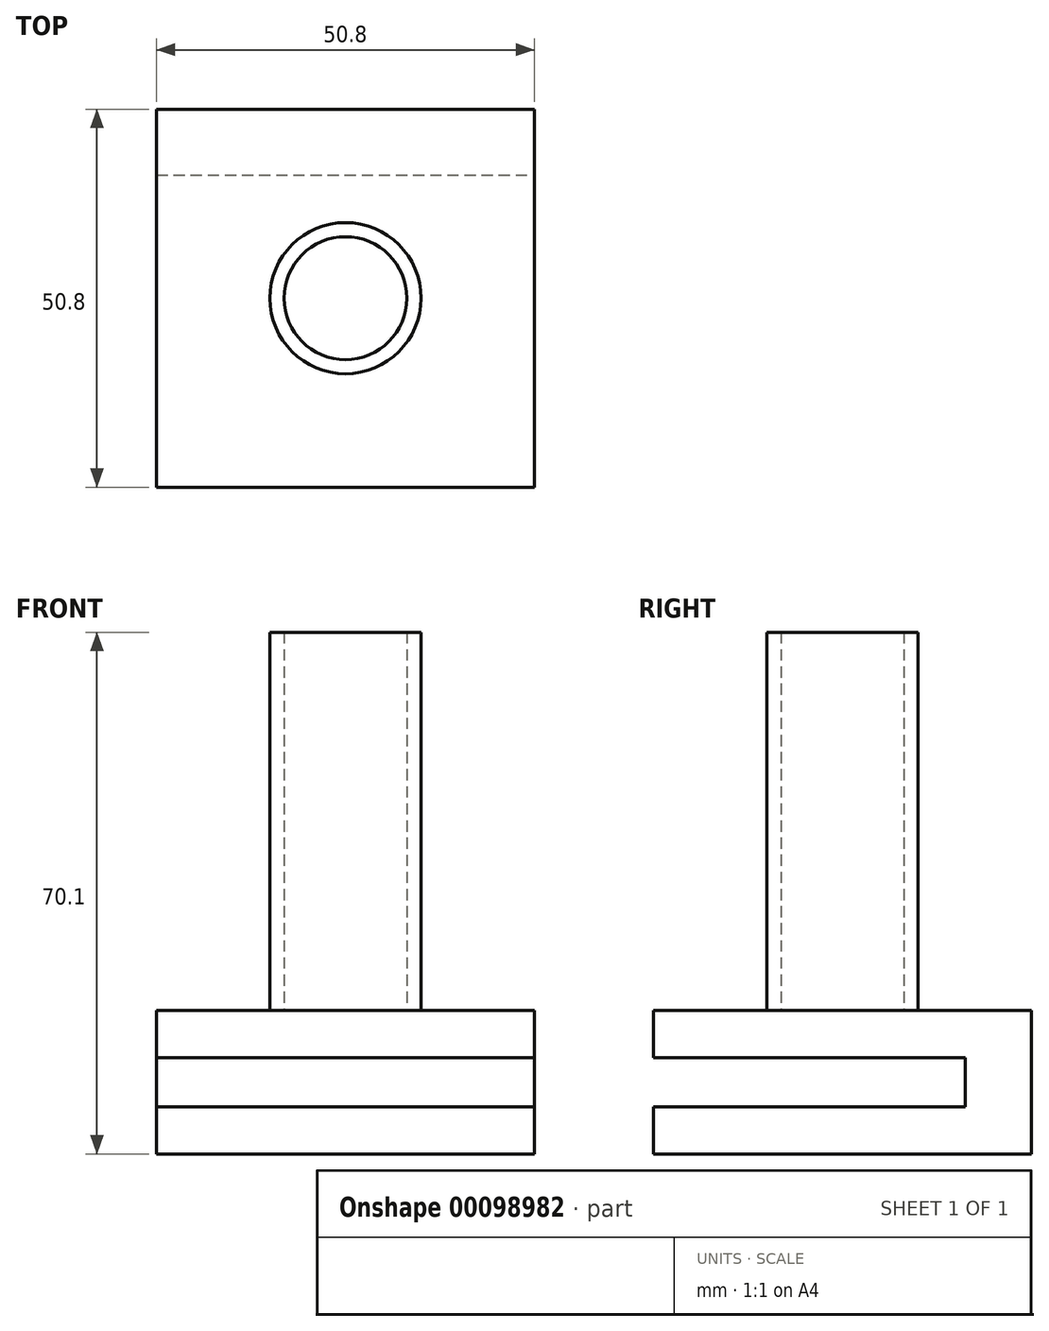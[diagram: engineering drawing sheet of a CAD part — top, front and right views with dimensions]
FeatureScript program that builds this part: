
annotation { "Feature Type Name" : "Feature", "Feature Type Description" : "" }
export const myFeature = defineFeature(function(context is Context, id is Id, definition is map)
    precondition{}
    {
        {
            var Q0;
            Q0=qCreatedBy(makeId("Top.planeOp"),FACE);
            var sketch = newSketch(context, id + "F0", { "sketchPlane" : qUnion([Q0])});
            skLineSegment(sketch, "E0.bottom", {"start": v(25.4, 25.4) * mm, "end": v(-25.4, 25.4) * mm});
            skLineSegment(sketch, "E0.top", {"start": v(25.4, -25.4) * mm, "end": v(-25.4, -25.4) * mm});
            skLineSegment(sketch, "E0.left", {"start": v(25.4, 25.4) * mm, "end": v(25.4, -25.4) * mm});
            skLineSegment(sketch, "E0.right", {"start": v(-25.4, 25.4) * mm, "end": v(-25.4, -25.4) * mm});
            skPoint(sketch, "E0.middle", {"position": v(0, 0) * mm});
            skSolve(sketch);
        }
        {
            var Q0;
            Q0=qSketchRegion(id+"F0",true);
            extrude(context, id + "F1", {"entities" : qUnion([Q0]), "depth" : 6.35 * mm});
        }
        {
            var Q0;
            Q0=makeQuery(id+"F1.opExtrude","CAP_FACE",FACE,{"disambiguationData":[OSD([sQuery(id+"F0.wireOp",EDGE,"E0.bottom"),sQuery(id+"F0.wireOp",EDGE,"E0.top"),sQuery(id+"F0.wireOp",EDGE,"E0.left"),sQuery(id+"F0.wireOp",EDGE,"E0.right")])],"isStart":false});
            var sketch = newSketch(context, id + "F2", { "sketchPlane" : qUnion([Q0])});
            skLineSegment(sketch, "E1.bottom", {"start": v(-25.4, 25.4) * mm, "end": v(25.4, 25.4) * mm});
            skLineSegment(sketch, "E1.top", {"start": v(-25.4, 16.53) * mm, "end": v(25.4, 16.53) * mm});
            skLineSegment(sketch, "E1.left", {"start": v(-25.4, 25.4) * mm, "end": v(-25.4, 16.53) * mm});
            skLineSegment(sketch, "E1.right", {"start": v(25.4, 25.4) * mm, "end": v(25.4, 16.53) * mm});
            skSolve(sketch);
        }
        {
            var Q0;
            Q0=qSketchRegion(id+"F2",true);
            extrude(context, id + "F3", {"entities" : qUnion([Q0]), "operationType" : NewBodyOperationType.ADD, "depth" : 6.6 * mm});
        }
        {
            var Q0;
            Q0=makeQuery(id+"F3.opExtrude","CAP_FACE",FACE,{"disambiguationData":[OSD([sQuery(id+"F2.wireOp",EDGE,"E1.bottom"),sQuery(id+"F2.wireOp",EDGE,"E1.top"),sQuery(id+"F2.wireOp",EDGE,"E1.left"),sQuery(id+"F2.wireOp",EDGE,"E1.right")])],"isStart":false});
            var sketch = newSketch(context, id + "F4", { "sketchPlane" : qUnion([Q0])});
            skLineSegment(sketch, "E2.bottom", {"start": v(-25.4, 25.4) * mm, "end": v(25.4, 25.4) * mm});
            skLineSegment(sketch, "E2.top", {"start": v(-25.4, -25.4) * mm, "end": v(25.4, -25.4) * mm});
            skLineSegment(sketch, "E2.left", {"start": v(-25.4, 25.4) * mm, "end": v(-25.4, -25.4) * mm});
            skLineSegment(sketch, "E2.right", {"start": v(25.4, 25.4) * mm, "end": v(25.4, -25.4) * mm});
            skSolve(sketch);
        }
        {
            var Q0;
            Q0=qSketchRegion(id+"F4",true);
            extrude(context, id + "F5", {"entities" : qUnion([Q0]), "operationType" : NewBodyOperationType.ADD, "depth" : 6.35 * mm});
        }
        {
            var Q0;
            Q0=makeQuery(id+"F5.opExtrude","CAP_FACE",FACE,{"disambiguationData":[OSD([sQuery(id+"F4.wireOp",EDGE,"E2.bottom"),sQuery(id+"F4.wireOp",EDGE,"E2.top"),sQuery(id+"F4.wireOp",EDGE,"E2.left"),sQuery(id+"F4.wireOp",EDGE,"E2.right")])],"isStart":false});
            var sketch = newSketch(context, id + "F6", { "sketchPlane" : qUnion([Q0])});
            skCircle(sketch, "E3", {"center": v(0, 0) * mm, "radius": 10.16 * mm});
            skCircle(sketch, "E4", {"center": v(0, 0) * mm, "radius": 8.26 * mm});
            skSolve(sketch);
        }
        {
            var Q0;
            Q0=qSketchRegion(id+"F6",true);
            extrude(context, id + "F7", {"entities" : qUnion([Q0]), "operationType" : NewBodyOperationType.ADD, "depth" : 50.8 * mm});
        }
    });
